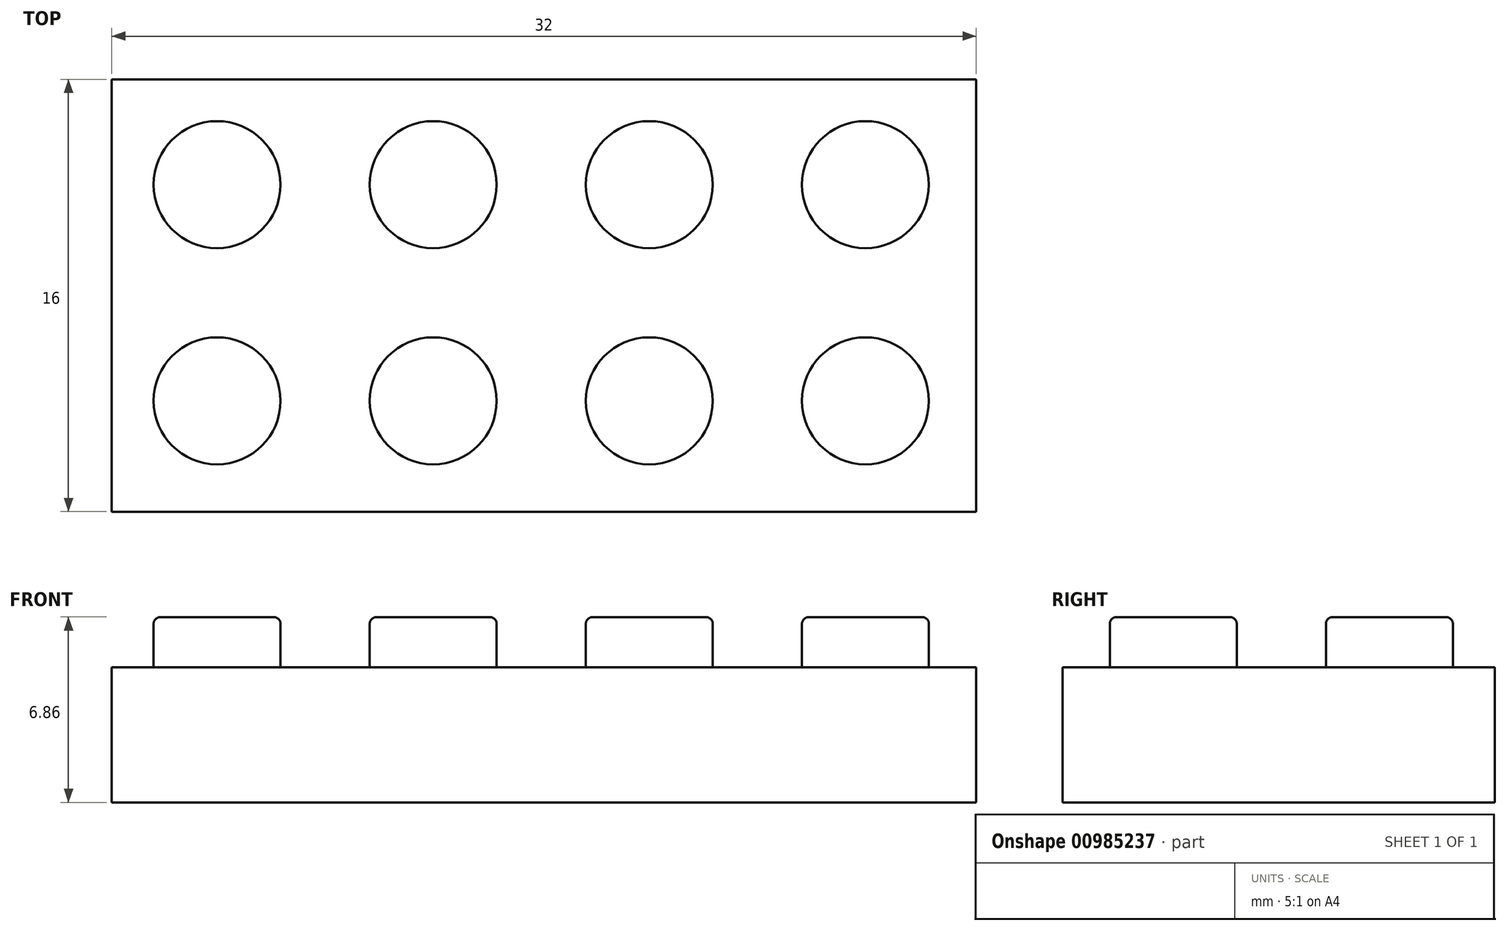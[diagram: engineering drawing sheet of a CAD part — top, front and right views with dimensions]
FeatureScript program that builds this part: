
annotation { "Feature Type Name" : "Feature", "Feature Type Description" : "" }
export const myFeature = defineFeature(function(context is Context, id is Id, definition is map)
    precondition{}
    {
        {
            var Q0;
            Q0=qCreatedBy(makeId("Top.planeOp"),FACE);
            var sketch = newSketch(context, id + "F0", { "sketchPlane" : qUnion([Q0])});
            skLineSegment(sketch, "E0.bottom", {"start": v(0, 0) * mm, "end": v(32, 0) * mm});
            skLineSegment(sketch, "E0.top", {"start": v(0, -16) * mm, "end": v(32, -16) * mm});
            skLineSegment(sketch, "E0.left", {"start": v(0, 0) * mm, "end": v(0, -16) * mm});
            skLineSegment(sketch, "E0.right", {"start": v(32, 0) * mm, "end": v(32, -16) * mm});
            skSolve(sketch);
        }
        {
            var Q0;
            Q0=makeQuery(id+"F0.imprint","IMPRINT",FACE,{"disambiguationData":[TD([[makeQuery(id+"F0.imprint","IMPRINT",EDGE,{"derivedFrom":sQuery(id+"F0.wireOp",EDGE,"E0.bottom")}),-1.0]])]});
            extrude(context, id + "F1", {"entities" : qUnion([Q0]), "depth" : 5 * mm, "offsetDistance" : 25.4 * mm});
        }
        {
            var Q0;
            Q0=makeQuery(id+"F1.opExtrude","CAP_FACE",FACE,{"disambiguationData":[OSD([sQuery(id+"F0.wireOp",EDGE,"E0.bottom"),sQuery(id+"F0.wireOp",EDGE,"E0.top"),sQuery(id+"F0.wireOp",EDGE,"E0.left"),sQuery(id+"F0.wireOp",EDGE,"E0.right")])],"isStart":false});
            var sketch = newSketch(context, id + "F2", { "sketchPlane" : qUnion([Q0])});
            skCircle(sketch, "E1", {"center": v(3.9, -3.9) * mm, "radius": 2.35 * mm});
            skCircle(sketch, "E2.0.1.0", {"center": v(3.9, -11.9) * mm, "radius": 2.35 * mm});
            skCircle(sketch, "E2.1.0.0", {"center": v(11.9, -3.9) * mm, "radius": 2.35 * mm});
            skCircle(sketch, "E2.1.1.0", {"center": v(11.9, -11.9) * mm, "radius": 2.35 * mm});
            skCircle(sketch, "E2.2.0.0", {"center": v(19.9, -3.9) * mm, "radius": 2.35 * mm});
            skCircle(sketch, "E2.2.1.0", {"center": v(19.9, -11.9) * mm, "radius": 2.35 * mm});
            skCircle(sketch, "E2.3.0.0", {"center": v(27.9, -3.9) * mm, "radius": 2.35 * mm});
            skCircle(sketch, "E2.3.1.0", {"center": v(27.9, -11.9) * mm, "radius": 2.35 * mm});
            skLineSegment(sketch, "E2.direction1", {"start": v(3.9, -3.9) * mm, "end": v(11.9, -3.9) * mm, "construction": true});
            skLineSegment(sketch, "E2.direction2", {"start": v(3.9, -3.9) * mm, "end": v(3.9, -11.9) * mm, "construction": true});
            skSolve(sketch);
        }
        {
            var Q0;
            Q0=makeQuery(id+"F2.imprint","IMPRINT",FACE,{"disambiguationData":[TD([[makeQuery(id+"F2.imprint","IMPRINT",EDGE,{"derivedFrom":sQuery(id+"F2.wireOp",EDGE,"E2.1.0.0")}),1.0]])]});
            var Q1;
            Q1=makeQuery(id+"F2.imprint","IMPRINT",FACE,{"disambiguationData":[TD([[makeQuery(id+"F2.imprint","IMPRINT",EDGE,{"derivedFrom":sQuery(id+"F2.wireOp",EDGE,"E1")}),1.0]])]});
            var Q2;
            Q2=makeQuery(id+"F2.imprint","IMPRINT",FACE,{"disambiguationData":[TD([[makeQuery(id+"F2.imprint","IMPRINT",EDGE,{"derivedFrom":sQuery(id+"F2.wireOp",EDGE,"E2.0.1.0")}),1.0]])]});
            var Q3;
            Q3=makeQuery(id+"F2.imprint","IMPRINT",FACE,{"disambiguationData":[TD([[makeQuery(id+"F2.imprint","IMPRINT",EDGE,{"derivedFrom":sQuery(id+"F2.wireOp",EDGE,"E2.1.1.0")}),1.0]])]});
            var Q4;
            Q4=makeQuery(id+"F2.imprint","IMPRINT",FACE,{"disambiguationData":[TD([[makeQuery(id+"F2.imprint","IMPRINT",EDGE,{"derivedFrom":sQuery(id+"F2.wireOp",EDGE,"E2.2.1.0")}),1.0]])]});
            var Q5;
            Q5=makeQuery(id+"F2.imprint","IMPRINT",FACE,{"disambiguationData":[TD([[makeQuery(id+"F2.imprint","IMPRINT",EDGE,{"derivedFrom":sQuery(id+"F2.wireOp",EDGE,"E2.2.0.0")}),1.0]])]});
            var Q6;
            Q6=makeQuery(id+"F2.imprint","IMPRINT",FACE,{"disambiguationData":[TD([[makeQuery(id+"F2.imprint","IMPRINT",EDGE,{"derivedFrom":sQuery(id+"F2.wireOp",EDGE,"E2.3.0.0")}),1.0]])]});
            var Q7;
            Q7=makeQuery(id+"F2.imprint","IMPRINT",FACE,{"disambiguationData":[TD([[makeQuery(id+"F2.imprint","IMPRINT",EDGE,{"derivedFrom":sQuery(id+"F2.wireOp",EDGE,"E2.3.1.0")}),1.0]])]});
            extrude(context, id + "F3", {"entities" : qUnion([Q0, Q1, Q2, Q3, Q4, Q5, Q6, Q7]), "operationType" : NewBodyOperationType.ADD, "depth" : 1.85 * mm, "offsetDistance" : 25.4 * mm});
        }
        {
            var Q0;
            Q0=makeQuery(id+"F3.opExtrude","CAP_FACE",FACE,{"disambiguationData":[OSD([sQuery(id+"F2.wireOp",EDGE,"E2.0.1.0")])],"isStart":false});
            var Q1;
            Q1=makeQuery(id+"F3.opExtrude","CAP_FACE",FACE,{"disambiguationData":[OSD([sQuery(id+"F2.wireOp",EDGE,"E1")])],"isStart":false});
            var Q2;
            Q2=makeQuery(id+"F3.opExtrude","CAP_FACE",FACE,{"disambiguationData":[OSD([sQuery(id+"F2.wireOp",EDGE,"E2.1.0.0")])],"isStart":false});
            var Q3;
            Q3=makeQuery(id+"F3.opExtrude","CAP_FACE",FACE,{"disambiguationData":[OSD([sQuery(id+"F2.wireOp",EDGE,"E2.1.1.0")])],"isStart":false});
            var Q4;
            Q4=makeQuery(id+"F3.opExtrude","CAP_FACE",FACE,{"disambiguationData":[OSD([sQuery(id+"F2.wireOp",EDGE,"E2.2.1.0")])],"isStart":false});
            var Q5;
            Q5=makeQuery(id+"F3.opExtrude","CAP_FACE",FACE,{"disambiguationData":[OSD([sQuery(id+"F2.wireOp",EDGE,"E2.2.0.0")])],"isStart":false});
            var Q6;
            Q6=makeQuery(id+"F3.opExtrude","CAP_FACE",FACE,{"disambiguationData":[OSD([sQuery(id+"F2.wireOp",EDGE,"E2.3.0.0")])],"isStart":false});
            var Q7;
            Q7=makeQuery(id+"F3.opExtrude","CAP_FACE",FACE,{"disambiguationData":[OSD([sQuery(id+"F2.wireOp",EDGE,"E2.3.1.0")])],"isStart":false});
            fillet(context, id + "F4", {"entities" : qUnion([Q0, Q1, Q2, Q3, Q4, Q5, Q6, Q7]), "radius" : 0.25 * mm, "tangentPropagation" : true, "allowEdgeOverflow" : false});
        }
    });
